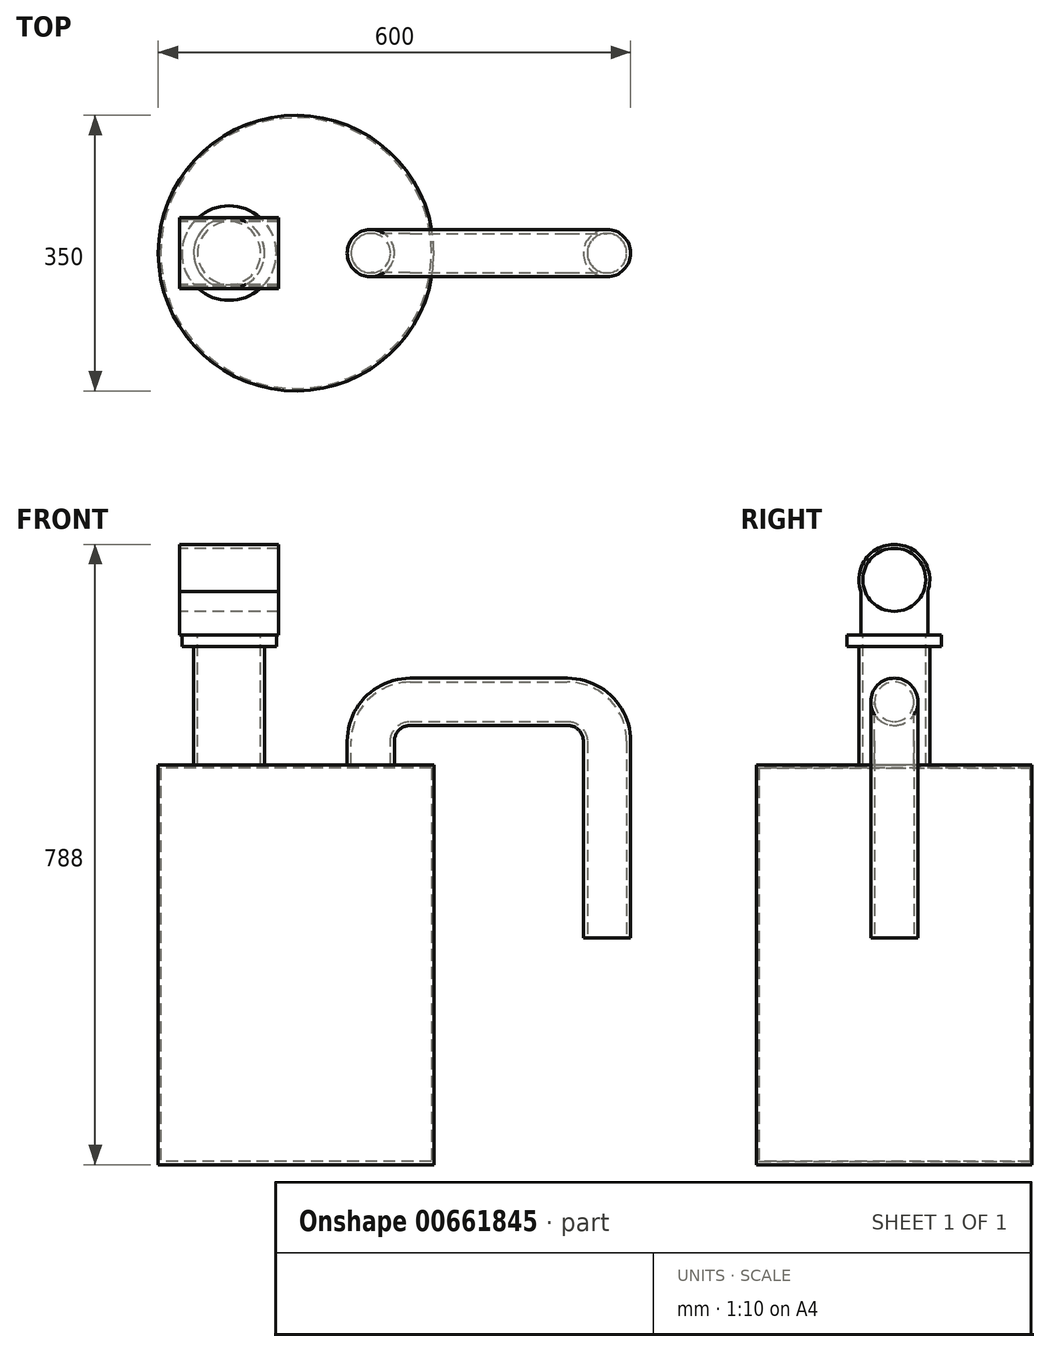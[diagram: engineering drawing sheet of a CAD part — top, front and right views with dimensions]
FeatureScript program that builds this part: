
annotation { "Feature Type Name" : "Feature", "Feature Type Description" : "" }
export const myFeature = defineFeature(function(context is Context, id is Id, definition is map)
    precondition{}
    {
        {
            var Q0;
            Q0=qCreatedBy(makeId("Top.planeOp"),FACE);
            var sketch = newSketch(context, id + "F0", { "sketchPlane" : qUnion([Q0])});
            skCircle(sketch, "E0", {"center": v(0, 0) * mm, "radius": 175 * mm});
            skCircle(sketch, "E1.0", {"center": v(0, 0) * mm, "radius": 172 * mm});
            skSolve(sketch);
        }
        {
            var Q0;
            Q0=makeQuery(id+"F0.imprint","IMPRINT",FACE,{"disambiguationData":[TD([[makeQuery(id+"F0.imprint","IMPRINT",EDGE,{"derivedFrom":sQuery(id+"F0.wireOp",EDGE,"E0")}),1.0]])]});
            extrude(context, id + "F1", {"entities" : qUnion([Q0]), "depth" : 500 * mm, "offsetDistance" : 25 * mm});
        }
        {
            var Q0;
            Q0=makeQuery(id+"F0.imprint","IMPRINT",FACE,{"disambiguationData":[TD([[makeQuery(id+"F0.imprint","IMPRINT",EDGE,{"derivedFrom":sQuery(id+"F0.wireOp",EDGE,"E1.0")}),1.0]])]});
            var Q1;
            Q1=makeQuery(id+"F0.imprint","IMPRINT",FACE,{"disambiguationData":[TD([[makeQuery(id+"F0.imprint","IMPRINT",EDGE,{"derivedFrom":sQuery(id+"F0.wireOp",EDGE,"E0")}),1.0]])]});
            extrude(context, id + "F2", {"entities" : qUnion([Q0, Q1]), "operationType" : NewBodyOperationType.ADD, "oppositeDirection" : true, "depth" : 4 * mm, "offsetDistance" : 25 * mm});
        }
        {
            var Q0;
            Q0=makeQuery(id+"F1.opExtrude","CAP_FACE",FACE,{"disambiguationData":[OSD([sQuery(id+"F0.wireOp",EDGE,"E0"),sQuery(id+"F0.wireOp",EDGE,"E1.0")])],"isStart":false});
            var sketch = newSketch(context, id + "F3", { "sketchPlane" : qUnion([Q0])});
            skCircle(sketch, "E2.0", {"center": v(0, 0) * mm, "radius": 175 * mm});
            skSolve(sketch);
        }
        {
            var Q0;
            Q0=makeQuery(id+"F3.imprint","IMPRINT",FACE,{"disambiguationData":[TD([[makeQuery(id+"F3.imprint","IMPRINT",EDGE,{"derivedFrom":sQuery(id+"F3.wireOp",EDGE,"E2.0")}),1.0]])]});
            var Q1;
            Q1=makeQuery(id+"F3.imprint","IMPRINT",FACE,{"disambiguationData":[TD([[makeQuery(id+"F3.imprint","IMPRINT",EDGE,{"derivedFrom":makeQuery(id+"F1.opExtrude","CAP_EDGE",EDGE,{"disambiguationData":[OSD([sQuery(id+"F0.wireOp",EDGE,"E1.0")])],"isStart":false})}),1.0]])]});
            extrude(context, id + "F4", {"entities" : qUnion([Q0, Q1]), "operationType" : NewBodyOperationType.ADD, "depth" : 4 * mm, "offsetDistance" : 25 * mm});
        }
        {
            var Q0;
            Q0=makeQuery(id+"F4.opExtrude","CAP_FACE",FACE,{"disambiguationData":[OSD([sQuery(id+"F3.wireOp",EDGE,"E2.0")])],"isStart":false});
            var sketch = newSketch(context, id + "F5", { "sketchPlane" : qUnion([Q0])});
            skCircle(sketch, "E3", {"center": v(-85, 0) * mm, "radius": 40 * mm});
            skCircle(sketch, "E4", {"center": v(95, 0) * mm, "radius": 25 * mm});
            skCircle(sketch, "E5.0", {"center": v(-85, 0) * mm, "radius": 45 * mm});
            skCircle(sketch, "E6.0", {"center": v(95, 0) * mm, "radius": 30 * mm});
            skLineSegment(sketch, "E7", {"start": v(0, 0) * mm, "end": v(175, 0) * mm, "construction": true});
            skSolve(sketch);
        }
        {
            var Q0;
            Q0=sQuery(id+"F5.wireOp",EDGE,"E7");
            cPlane(context, id + "F6", {"entities" : qUnion([Q0]), "cplaneType" : CPlaneType.LINE_ANGLE, "offset" : 25 * mm, "angle" : 0 * degree, "width" : 150 * mm, "height" : 150 * mm});
        }
        {
            var Q0;
            Q0=qCreatedBy(id+"F6.planeOp",FACE);
            var sketch = newSketch(context, id + "F7", { "sketchPlane" : qUnion([Q0])});
            skPoint(sketch, "E8.0", {"position": v(85, 504) * mm});
            skPoint(sketch, "E9.0", {"position": v(-95, 504) * mm});
            skLineSegment(sketch, "E10", {"start": v(85, 504) * mm, "end": v(85, 654) * mm});
            skLineSegment(sketch, "E11", {"start": v(-95, 504) * mm, "end": v(-95, 534) * mm});
            skLineSegment(sketch, "E12", {"start": v(-145, 584) * mm, "end": v(-345, 584) * mm});
            skLineSegment(sketch, "E13", {"start": v(-395, 534) * mm, "end": v(-395, 284) * mm});
            skPoint(sketch, "E14.visualSharp", {"position": v(-95, 584) * mm});
            skArc(sketch, "E14.filletArc", {"start": v(-95, 534) * mm, "mid": v(-109.64, 569.36) * mm, "end": v(-145, 584) * mm});
            skPoint(sketch, "E15.visualSharp", {"position": v(-395, 584) * mm});
            skArc(sketch, "E15.filletArc", {"start": v(-345, 584) * mm, "mid": v(-380.36, 569.36) * mm, "end": v(-395, 534) * mm});
            skSolve(sketch);
        }
        {
            var Q0;
            Q0=makeQuery(id+"F5.imprint","IMPRINT",FACE,{"disambiguationData":[TD([[makeQuery(id+"F5.imprint","IMPRINT",EDGE,{"derivedFrom":sQuery(id+"F5.wireOp",EDGE,"E4")}),-1.0]])]});
            var Q1;
            Q1=sQuery(id+"F7.wireOp",EDGE,"E11");
            var Q2;
            Q2=sQuery(id+"F7.wireOp",EDGE,"E14.filletArc");
            var Q3;
            Q3=sQuery(id+"F7.wireOp",EDGE,"E12");
            var Q4;
            Q4=sQuery(id+"F7.wireOp",EDGE,"E15.filletArc");
            var Q5;
            Q5=sQuery(id+"F7.wireOp",EDGE,"E13");
            sweep(context, id + "F8", {"operationType" : NewBodyOperationType.ADD, "profiles" : qUnion([Q0]), "path" : qUnion([Q1, Q2, Q3, Q4, Q5])});
        }
        {
            var Q0;
            Q0=makeQuery(id+"F5.imprint","IMPRINT",FACE,{"disambiguationData":[TD([[makeQuery(id+"F5.imprint","IMPRINT",EDGE,{"derivedFrom":sQuery(id+"F5.wireOp",EDGE,"E3")}),-1.0]])]});
            var Q1;
            Q1=sQuery(id+"F7.wireOp",EDGE,"E10");
            sweep(context, id + "F9", {"operationType" : NewBodyOperationType.ADD, "profiles" : qUnion([Q0]), "path" : qUnion([Q1])});
        }
        {
            var Q0;
            Q0=makeQuery(id+"F9.opSweep","CAP_FACE",FACE,{"disambiguationData":[OSD([sQuery(id+"F5.wireOp",EDGE,"E3"),sQuery(id+"F5.wireOp",EDGE,"E5.0"),sQuery(id+"F7.wireOp",VERTEX,"E10.end")])],"isStart":false});
            var sketch = newSketch(context, id + "F10", { "sketchPlane" : qUnion([Q0])});
            skCircle(sketch, "E16.0", {"center": v(-85, 0) * mm, "radius": 45 * mm});
            skCircle(sketch, "E17.0", {"center": v(-85, 0) * mm, "radius": 60 * mm});
            skLineSegment(sketch, "E18", {"start": v(-85, 0) * mm, "end": v(-85, -60) * mm});
            skSolve(sketch);
        }
        {
            var Q0;
            Q0 = qSketchRegion(id + "F10", true);
            var Q1;
            Q1=makeQuery(id+"F10.imprint","IMPRINT",FACE,{"disambiguationData":[TD([[makeQuery(id+"F10.imprint","IMPRINT",EDGE,{"derivedFrom":sQuery(id+"F10.wireOp",EDGE,"E16.0")}),1.0]])]});
            extrude(context, id + "F11", {"entities" : qUnion([Q0, Q1]), "operationType" : NewBodyOperationType.ADD, "depth" : 15 * mm, "offsetDistance" : 25 * mm});
        }
        {
            var Q0;
            Q0=sQuery(id+"F10.wireOp",EDGE,"E18");
            cPlane(context, id + "F12", {"entities" : qUnion([Q0]), "cplaneType" : CPlaneType.LINE_ANGLE, "offset" : 25 * mm, "angle" : 90 * degree, "width" : 150 * mm, "height" : 150 * mm});
        }
        {
            var Q0;
            Q0=qCreatedBy(id+"F12.planeOp",FACE);
            var sketch = newSketch(context, id + "F13", { "sketchPlane" : qUnion([Q0])});
            skCircle(sketch, "E19", {"center": v(0, 739) * mm, "radius": 45 * mm});
            skCircle(sketch, "E20.0", {"center": v(0, 739) * mm, "radius": 40 * mm});
            skLineSegment(sketch, "E21.0", {"start": v(-60, 669) * mm, "end": v(60, 669) * mm});
            skLineSegment(sketch, "E22", {"start": v(42.5, 724.2) * mm, "end": v(42.5, 669) * mm});
            skLineSegment(sketch, "E23", {"start": v(-42.5, 724.2) * mm, "end": v(-42.5, 669) * mm});
            skLineSegment(sketch, "E24", {"start": v(0, 739) * mm, "end": v(0, 711.6) * mm, "construction": true});
            skSolve(sketch);
        }
        {
            var Q0;
            {var subQ0=sQuery(id+"F13.wireOp",EDGE,"E22");Q0=makeQuery(id+"F13.imprint","IMPRINT",FACE,{"disambiguationData":[TD([[makeQuery(id+"F13.imprint","IMPRINT",EDGE,{"derivedFrom":subQ0}),-1.0]])]});}
            var Q1;
            Q1=makeQuery(id+"F13.imprint","IMPRINT",FACE,{"disambiguationData":[TD([[makeQuery(id+"F13.imprint","IMPRINT",EDGE,{"derivedFrom":sQuery(id+"F13.wireOp",EDGE,"E20.0")}),-1.0]])]});
            extrude(context, id + "F14", {"entities" : qUnion([Q0, Q1]), "operationType" : NewBodyOperationType.ADD, "endBound" : BoundingType.SYMMETRIC, "depth" : 125.8 * mm, "offsetDistance" : 25 * mm});
        }
    });
